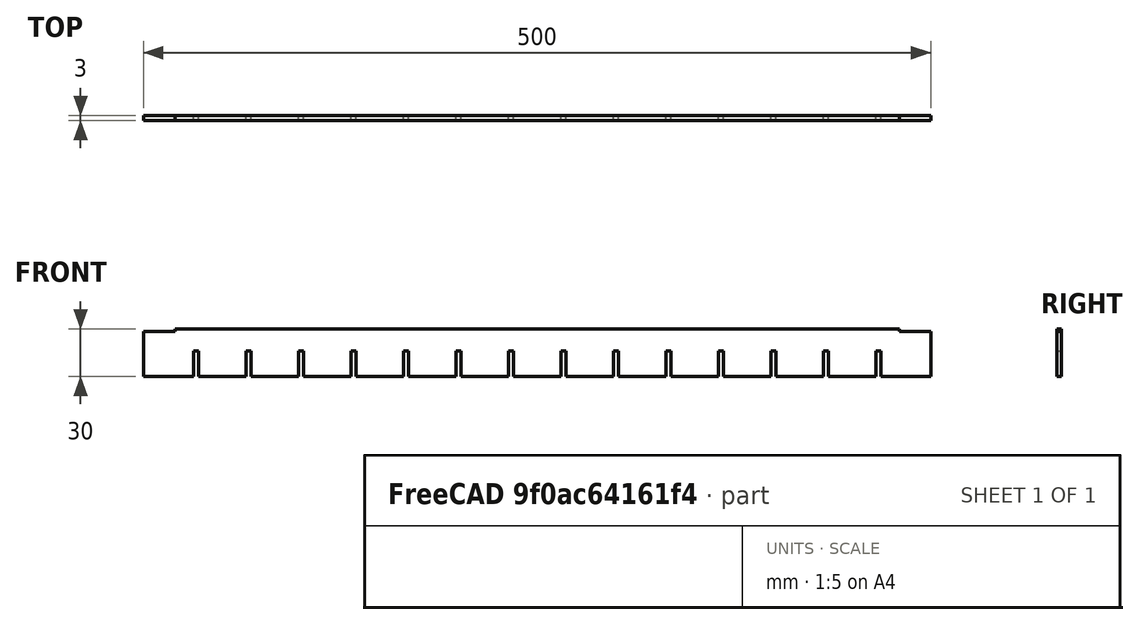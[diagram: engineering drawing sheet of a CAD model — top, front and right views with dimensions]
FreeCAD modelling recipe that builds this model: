
FCSTD DOCUMENT  (FreeCAD 0.16R6698 (Git))
Label: strip_500_double
License: CC-BY 3.0
LicenseURL: http://creativecommons.org/licenses/by/3.0/
objects: Part::Box×3, Part::FeaturePython×2, Part::Cut×2
note: 7 computed .brp shape members not serialized (recipe doc carries the construction recipe); baked Part::Feature solids carry a one-line shape summary decoded from their .brp

FEATURE [Part::Box] Box  label="Strip"
  Height = 30
  Length = 500
  Width = 3
  expr: Length = bottom#Length - 2 * bottom#Height
FEATURE [Part::Box] Box001  label="Hole"
  Height = 16
  Length = 3
  Placement = pos=(31.8333,0,0) rot=(0,0,1;0rad)
  Width = 3
  expr: Placement.Base.x = 100 / 3 - Strip.Width / 2mm
  expr: Height = Strip.Height / 2 + 1mm
  expr: Length = Strip.Width
  expr: Width = Strip.Width
FEATURE [Part::FeaturePython] Array  # Draft array (typed FeaturePython)
  Angle = 360
  ArrayType = 0
  Axis = (1,0,0)
  Base = -> Box001
  Center = (0,0,0)
  IntervalX = (33.3333,0,0)
  IntervalY = (0,1,0)
  IntervalZ = (0,0,1)
  NumberPolar = 1
  NumberX = 14
  NumberY = 0
  NumberZ = 0
  expr: IntervalX.x = 100 / 3
FEATURE [Part::Cut] Cut
  Base = -> Box
  Tool = -> Array
FEATURE [Part::Box] Box002  label="CablePassing"
  Height = 1.5
  Length = 20
  Placement = pos=(0,0,28.5) rot=(0,0,1;0rad)
  Width = 10
  expr: Placement.Base.z = Strip.Height - CablePassing.Height
FEATURE [Part::FeaturePython] Array001  label="CablePassings"  # Draft array (typed FeaturePython)
  Angle = 360
  ArrayType = 0
  Axis = (0,0,1)
  Base = -> Box002
  Center = (0,0,0)
  Fuse = false
  IntervalAxis = (0,0,0)
  IntervalX = (480,0,0)
  IntervalY = (0,1,0)
  IntervalZ = (0,0,0)
  NumberPolar = 1
  NumberX = 2
  NumberY = 1
  NumberZ = 1
  expr: IntervalX.x = Strip.Length - CablePassing.Length
FEATURE [Part::Cut] Cut001  label="PiercedStrip"
  Base = -> Cut
  Tool = -> Array001
